# Revit family: CADS_AIRFLOWdev_AirTerminal_RoundCowl_Exhaust
name_source: partatom
category: Air Terminals
revit_build: Autodesk Revit 2015 (Build: 20160512_0715(x64)
units: mm (PartAtom-declared; Revit-internal decimal feet)

## types (8) — shared parameters
6MonthlyMaintenance = Visually inspect system, clean the fan and ducting if necessary
AirflowRateRange = 0-61
AssetType = Fixed
CEApproval = Yes
Color = Silver
Constituents = Silver
Default Elevation = 1219 mm
DurationUnit = Years
Exclusions = Incorrect Use / Incorrect Installation / Installed by a non-accredited electrician. Customer abuse.
FaceType = LOUVERED
FlowControlType = NONE
Grade = Virgin
HasIntegralControl = No
HasSoundAttenuator = No
HasThermalInsulation = No
ISO140001 = Yes
ISO90001 = Yes
IsExtendedWarranty = No
Manufacturer = Airflow Developments Ltd
ManufacturerAddress = Aidelle House
Lancaster Road
Cressex Business Park
High Wycombe
Bucks
HP123QP
ManufacturerTelephone = 01494 525252
ManufacturerWebsite = www.airflow.com
Material = Stainless Steel
MountingType = SURFACE
NBSCode = 90-75-50/370 Air terminals;
PointOfContact = Airflow Developments Ltd
ProductionYear = 2017
RoundCowl = CADS_Airflow_Chrome
ServiceLifeDuration = 10
ServiceLifeType = EXPECTEDSERVICELIFE
Shape = Round
Uniclass2015 = Pr_65_70_46_01
WarrantyContent = Replacement of part if faulty
WarrantyGuarantor = Airflow Developments Ltd
WarrantyPeriod = 2
zero-valued in all types: NumberOfSlots

## per-type parameters (varying)
| type | A | Base | C | D | Description | E | GlobalTradeItemNumber | GrossWeight | ModelLabel | ModelReference | NominalHeight | NominalLength | NominalWidth | ReplacementCost | ShippingWeight | Size | Void |
| 100mm With Louvers | 150 mm | 130 mm  [stored 0.426509 ft] | 115 mm  [stored 0.377297 ft] | 100 mm  [stored 0.328084 ft] | 100mm dia round cowl complete with Internal louvers | 42 mm  [stored 0.137795 ft] | 5019009306346 | 0.03 kg | 100mm dia round cowl complete with Internal louvers | 52644501 | 150 mm | 115 mm  [stored 0.377297 ft] | 150 mm | 20.676 | 0.03 kg | 115 x 150 x 150 | 63 mm  [stored 0.206693 ft] |
| 125mm With Louvers | 180 mm  [stored 0.590551 ft] | 160 mm  [stored 0.524934 ft] | 145 mm  [stored 0.475722 ft] | 125 mm  [stored 0.410105 ft] | 125mm dia round cowl complete with internal louvers | 48 mm  [stored 0.15748 ft] | 5019009318011 | 0.04 kg | 125mm dia round cowl complete with internal louvers | 9041226 | 190 mm | 145 mm  [stored 0.475722 ft] | 190 mm | 30.228 | 0.04 kg | 145 x 190 x 190 | 78 mm  [stored 0.255906 ft] |
| 150mm With Louvers | 207 mm  [stored 0.679134 ft] | 187 mm | 155 mm  [stored 0.50853 ft] | 150 mm | 150mm dia round cowl complete with Internal louvers | 55 mm  [stored 0.180446 ft] | 5019009306360 | 0.05 kg | 150mm dia round cowl complete with Internal louvers | 52644601 | 210 mm  [stored 0.688976 ft] | 155 mm  [stored 0.50853 ft] | 210 mm  [stored 0.688976 ft] | 39.756 | 0.05 kg | 155 x 210 x 210 | 92 mm |
| 180mm With Louvers | 265 mm  [stored 0.869423 ft] | 245 mm  [stored 0.803806 ft] | 190 mm | 173 mm  [stored 0.567585 ft] | 180mm dia round cowl complete with internal louvers | 55 mm  [stored 0.180446 ft] | 5019009318028 | 0.08 kg | 180mm dia round cowl complete with internal louvers | 9041227 | 255 mm  [stored 0.836614 ft] | 195 mm  [stored 0.639764 ft] | 255 mm  [stored 0.836614 ft] | 60.444 | 0.09 kg | 195 x 255 x 255 | 121 mm |
| 100mm With Mesh | 150 mm | 130 mm  [stored 0.426509 ft] | 115 mm  [stored 0.377297 ft] | 100 mm  [stored 0.328084 ft] | 100mm dia round cowl complete with Internal mesh | 42 mm  [stored 0.137795 ft] | 5019009306384 | 0.03 kg | 100mm dia round cowl complete with Internal mesh | 52644701 | 150 mm | 115 mm  [stored 0.377297 ft] | 150 mm | 20.676 | 0.03 kg | 115 x 150 x 150 | 63 mm  [stored 0.206693 ft] |
| 125mm With Mesh | 180 mm  [stored 0.590551 ft] | 160 mm  [stored 0.524934 ft] | 145 mm  [stored 0.475722 ft] | 125 mm  [stored 0.410105 ft] | 125mm dia round cowl complete with internal mesh | 48 mm  [stored 0.15748 ft] | 5019009318035 | 0.04 kg | 125mm dia round cowl complete with internal mesh | 9041228 | 190 mm | 145 mm  [stored 0.475722 ft] | 190 mm | 30.228 | 0.04 kg | 145 x 190 x 190 | 78 mm  [stored 0.255906 ft] |
| 150mm With Mesh | 207 mm  [stored 0.679134 ft] | 187 mm | 155 mm  [stored 0.50853 ft] | 150 mm | 150mm dia round cowl complete with Internal mesh | 55 mm  [stored 0.180446 ft] | 5019009306407 | 0.05 kg | 150mm dia round cowl complete with Internal mesh | 52644801 | 210 mm  [stored 0.688976 ft] | 155 mm  [stored 0.50853 ft] | 210 mm  [stored 0.688976 ft] | 39.756 | 0.05 kg | 155 x 210 x 210 | 92 mm |
| 180mm With Mesh | 265 mm  [stored 0.869423 ft] | 245 mm  [stored 0.803806 ft] | 190 mm | 173 mm  [stored 0.567585 ft] | 180mm dia round cowl complete with internal mesh | 55 mm  [stored 0.180446 ft] | 5019009318042 | 0.08 kg | 180mm dia round cowl complete with internal mesh | 9041229 | 255 mm  [stored 0.836614 ft] | 195 mm  [stored 0.639764 ft] | 255 mm  [stored 0.836614 ft] | 60.444 | 0.09 kg | 195 x 255 x 255 | 121 mm |

note: [stored X ft] marks values corroborated as IEEE doubles in the binary element streams (Revit-internal decimal feet)

## geometry (parser evidence)
native form markers: Blend x12, Sweep x2
no freeform markers — native parametric forms only
